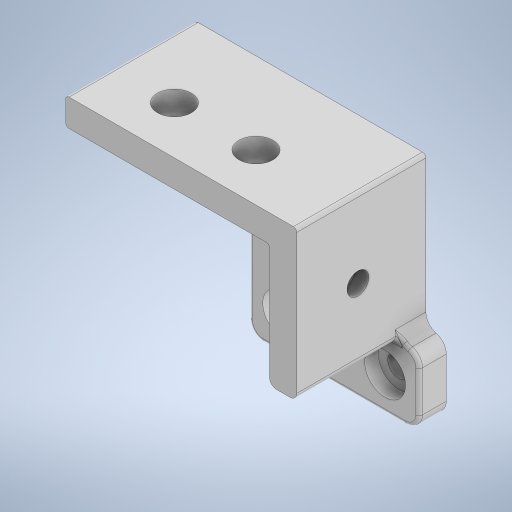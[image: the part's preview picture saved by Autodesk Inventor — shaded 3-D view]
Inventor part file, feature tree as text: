
AUTODESK INVENTOR PART (.ipt)
format: ipt  version: 2024.3 (Build 283343000, 343)  size: 505,344 bytes
history: native  units: mm
features: sketch x17, extrude x14, projected_geometry x7, fillet x4, hole x3, other x1, mirror x1
ambient origin geometry x8: Origin, YZ Plane, XZ Plane, XY Plane, X Axis, Y Axis, Z Axis, Center Point
bodies: Body1 (feature_tree)
feature tree (47):
  other  "ソリッド1"
  extrude  "押し出し1"  Depth=25.0mm
  hole  "穴1"  [1 undecoded]
  extrude  "押し出し2"  Depth=4.0mm TaperAngle=0.0deg
  extrude  "押し出し3"  Depth=15.0mm
  hole  "穴2"  [1 undecoded]
  extrude  "押し出し4"  Depth=5.0mm
  extrude  "押し出し5"  Depth=5.0mm
  extrude  "押し出し6"  Depth=3.0mm
  extrude  "押し出し7"  Depth=22.0mm TaperAngle=0.0deg
  extrude  "押し出し8"  Depth=4.0mm
  extrude  "押し出し9"  Depth=22.0mm TaperAngle=0.0deg
  extrude  "押し出し10"  Depth=10.5mm
  extrude  "押し出し11"  Depth=6.0mm
  hole  "穴4"  [1 undecoded]
  extrude  "押し出し12"  Depth=8.0mm
  extrude  "押し出し13"  Depth=6.0mm
  fillet  "フィレット1"  Radius=22.0mm
  fillet  "フィレット2"  Radius=3.0mm
  fillet  "フィレット3"  Radius=4.0mm
  fillet  "フィレット4"  Radius=3.0mm
  mirror  "ミラー1"
  extrude  "押し出し14"  Depth=20.0mm
  sketch  "スケッチ1"
  sketch  "スケッチ2"
  sketch  "スケッチ3"
  sketch  "スケッチ4"
  sketch  "スケッチ5"
  sketch  "スケッチ8"
  projected_geometry  "投影ループ1"
  sketch  "スケッチ9"
  sketch  "スケッチ10"
  projected_geometry  "投影ループ2"
  sketch  "スケッチ11"
  projected_geometry  "投影ループ3"
  sketch  "スケッチ12"
  projected_geometry  "投影ループ4"
  sketch  "スケッチ14"
  sketch  "スケッチ15"
  projected_geometry  "投影ループ5"
  sketch  "スケッチ16"
  projected_geometry  "投影ループ6"
  sketch  "スケッチ17"
  sketch  "スケッチ18"
  projected_geometry  "投影ループ7"
  sketch  "スケッチ19"
  sketch  "スケッチ20"
note: 3 required parameter values undecoded (feature->parameter linkage not recoverable at this tier; creation-order binding heuristic only, values carry confidence <= 0.55)
